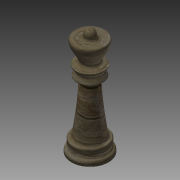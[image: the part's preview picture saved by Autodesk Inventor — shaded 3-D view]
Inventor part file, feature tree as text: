
AUTODESK INVENTOR PART (.ipt)
format: ipt  version: 2015 SP1 (Build 190203100, 203)  size: 396,288 bytes
history: native  units: mm
features: revolve x1, fillet x1, sketch x1
ambient origin geometry x8: Origin, YZ Plane, XZ Plane, XY Plane, X Axis, Y Axis, Z Axis, Center Point
bodies: Body1 (feature_tree)
feature tree (3):
  revolve  "Revolution2"  [1 undecoded]
  fillet  "Fillet6"  Radius=2.0mm
  sketch  "Sketch1"  dims[d11=2.0mm d13=1.0mm d24=2.0mm d35=2.0mm d39=85.0mm d40=90.0deg d41=2.0mm]
note: 1 required parameter value undecoded (feature->parameter linkage not recoverable at this tier; creation-order binding heuristic only, values carry confidence <= 0.55)
